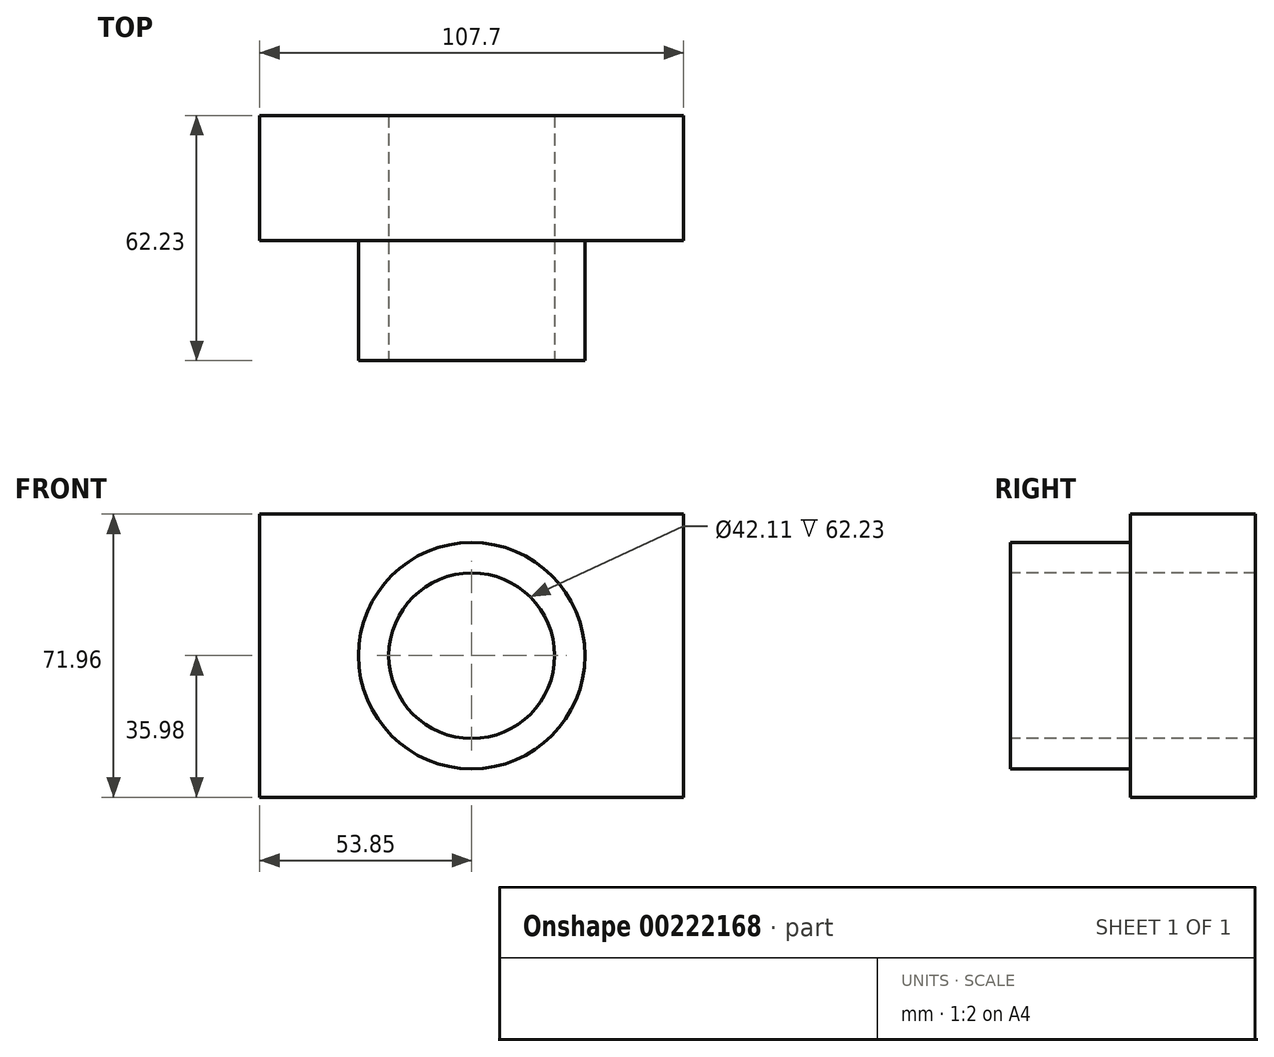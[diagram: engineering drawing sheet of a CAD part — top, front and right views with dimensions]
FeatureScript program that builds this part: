
annotation { "Feature Type Name" : "Feature", "Feature Type Description" : "" }
export const myFeature = defineFeature(function(context is Context, id is Id, definition is map)
    precondition{}
    {
        {
            var Q0;
            Q0=qCreatedBy(makeId("Front.planeOp"),FACE);
            var sketch = newSketch(context, id + "F0", { "sketchPlane" : qUnion([Q0])});
            skLineSegment(sketch, "E0.bottom", {"start": v(53.85, -35.98) * mm, "end": v(-53.85, -35.98) * mm});
            skLineSegment(sketch, "E0.top", {"start": v(53.85, 35.98) * mm, "end": v(-53.85, 35.98) * mm});
            skLineSegment(sketch, "E0.left", {"start": v(53.85, -35.98) * mm, "end": v(53.85, 35.98) * mm});
            skLineSegment(sketch, "E0.right", {"start": v(-53.85, -35.98) * mm, "end": v(-53.85, 35.98) * mm});
            skPoint(sketch, "E0.middle", {"position": v(0, 0) * mm});
            skSolve(sketch);
        }
        {
            var Q0;
            Q0=makeQuery(id+"F0.imprint","IMPRINT",FACE,{"disambiguationData":[TD([[makeQuery(id+"F0.imprint","IMPRINT",EDGE,{"derivedFrom":sQuery(id+"F0.wireOp",EDGE,"E0.bottom")}),-1.0]])]});
            extrude(context, id + "F1", {"entities" : qUnion([Q0]), "depth" : 31.75 * mm});
        }
        {
            var Q0;
            Q0=makeQuery(id+"F1.opExtrude","CAP_FACE",FACE,{"disambiguationData":[OSD([sQuery(id+"F0.wireOp",EDGE,"E0.bottom"),sQuery(id+"F0.wireOp",EDGE,"E0.top"),sQuery(id+"F0.wireOp",EDGE,"E0.left"),sQuery(id+"F0.wireOp",EDGE,"E0.right")])],"isStart":false});
            var sketch = newSketch(context, id + "F2", { "sketchPlane" : qUnion([Q0])});
            skCircle(sketch, "E1", {"center": v(0, 0) * mm, "radius": 28.76 * mm});
            skSolve(sketch);
        }
        {
            var Q0;
            Q0 = qSketchRegion(id + "F2", true);
            extrude(context, id + "F3", {"entities" : qUnion([Q0]), "operationType" : NewBodyOperationType.ADD, "depth" : 30.48 * mm});
        }
        {
            var Q0;
            Q0=makeQuery(id+"F3.opExtrude","CAP_FACE",FACE,{"disambiguationData":[OSD([sQuery(id+"F2.wireOp",EDGE,"E1")])],"isStart":false});
            var sketch = newSketch(context, id + "F4", { "sketchPlane" : qUnion([Q0])});
            skCircle(sketch, "E2", {"center": v(0, 0) * mm, "radius": 21.05 * mm});
            skSolve(sketch);
        }
        {
            var Q0;
            Q0 = qSketchRegion(id + "F4", true);
            extrude(context, id + "F5", {"entities" : qUnion([Q0]), "operationType" : NewBodyOperationType.REMOVE, "endBound" : BoundingType.THROUGH_ALL, "oppositeDirection" : true, "depth" : 25.4 * mm});
        }
    });
